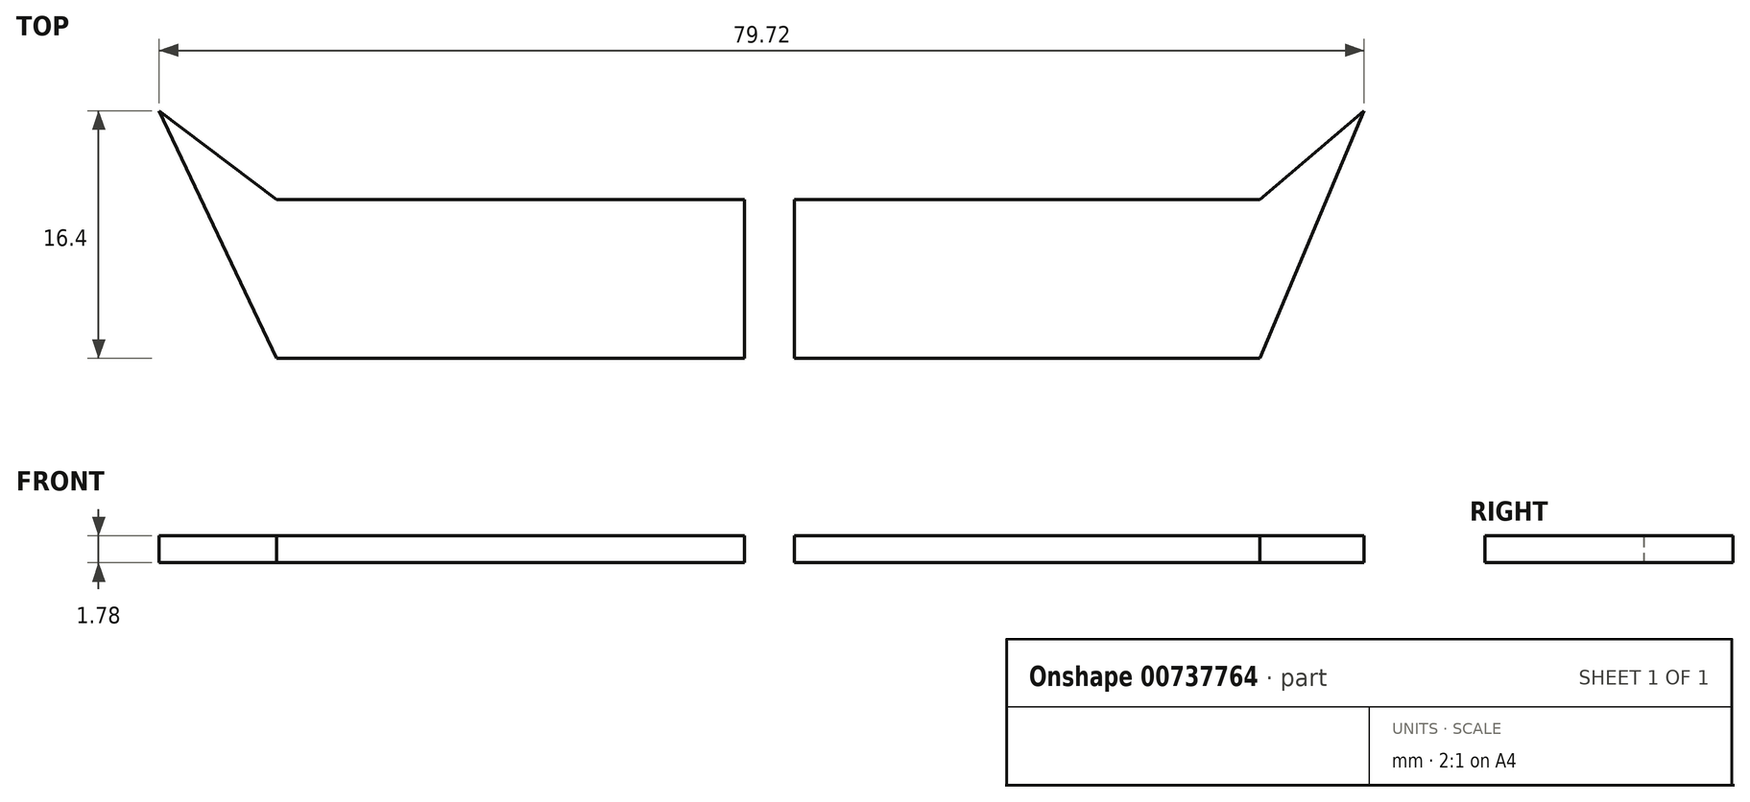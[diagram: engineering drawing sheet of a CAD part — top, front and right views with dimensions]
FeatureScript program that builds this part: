
annotation { "Feature Type Name" : "Feature", "Feature Type Description" : "" }
export const myFeature = defineFeature(function(context is Context, id is Id, definition is map)
    precondition{}
    {
        {
            var Q0;
            Q0=qCreatedBy(makeId("Top.planeOp"),FACE);
            var sketch = newSketch(context, id + "F0", { "sketchPlane" : qUnion([Q0])});
            skLineSegment(sketch, "E0", {"start": v(0, 0) * mm, "end": v(-30.94, 0) * mm});
            skLineSegment(sketch, "E1", {"start": v(3.3, 0) * mm, "end": v(34.1, 0) * mm});
            skLineSegment(sketch, "E2", {"start": v(34.1, 0) * mm, "end": v(41.01, 5.9) * mm});
            skLineSegment(sketch, "E3", {"start": v(41.01, 5.9) * mm, "end": v(34.1, -10.5) * mm});
            skLineSegment(sketch, "E4", {"start": v(34.1, -10.5) * mm, "end": v(3.3, -10.5) * mm});
            skLineSegment(sketch, "E5", {"start": v(3.3, -10.5) * mm, "end": v(3.3, 0) * mm});
            skLineSegment(sketch, "E6", {"start": v(-30.94, 0) * mm, "end": v(-38.7, 5.9) * mm});
            skLineSegment(sketch, "E7", {"start": v(-38.7, 5.9) * mm, "end": v(-30.94, -10.5) * mm});
            skLineSegment(sketch, "E8", {"start": v(-30.94, -10.5) * mm, "end": v(0, -10.5) * mm});
            skLineSegment(sketch, "E9", {"start": v(0, -10.5) * mm, "end": v(0, 0) * mm});
            skLineSegment(sketch, "E10", {"start": v(-30.94, 0) * mm, "end": v(0, 0) * mm});
            skSolve(sketch);
        }
        {
            var Q0;
            Q0 = qSketchRegion(id + "F0", true);
            extrude(context, id + "F1", {"entities" : qUnion([Q0]), "depth" : 1.78 * mm, "offsetDistance" : 25.4 * mm});
        }
    });
